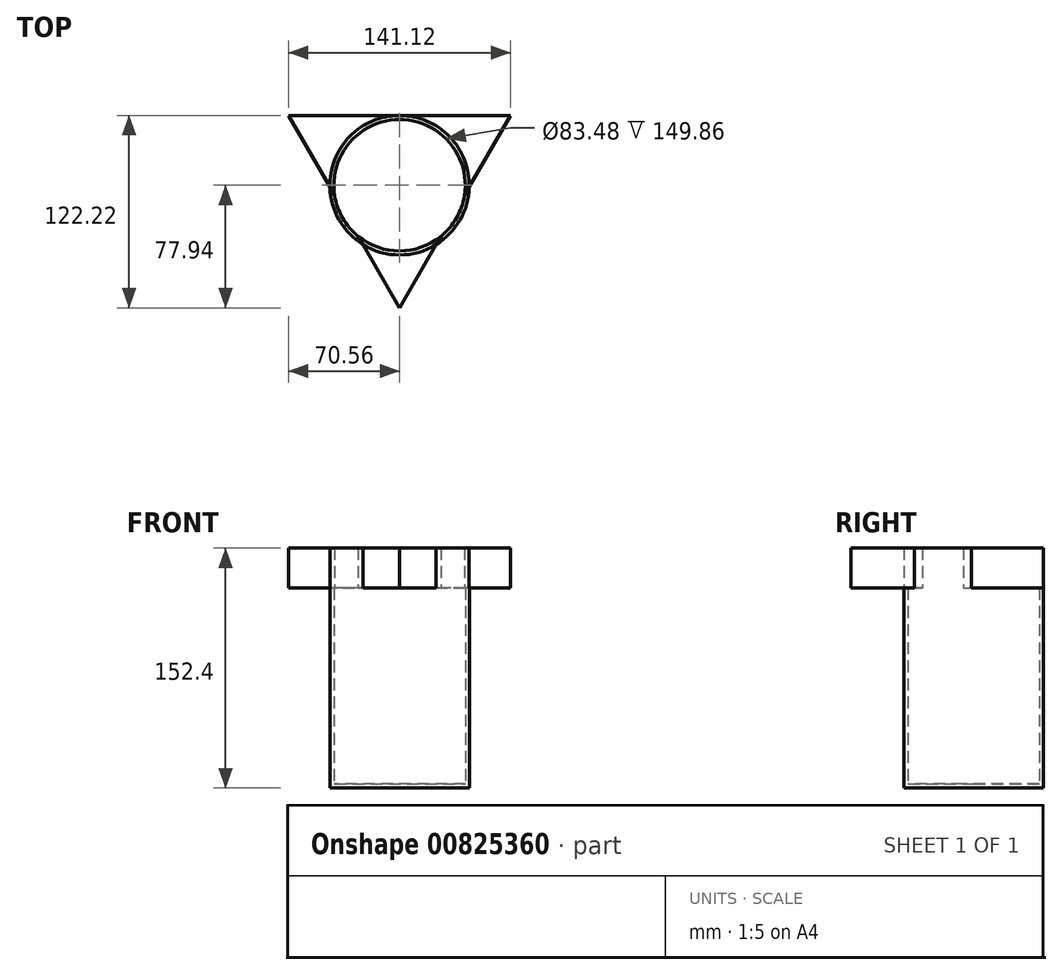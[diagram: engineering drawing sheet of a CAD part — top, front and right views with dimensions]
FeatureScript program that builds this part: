
annotation { "Feature Type Name" : "Feature", "Feature Type Description" : "" }
export const myFeature = defineFeature(function(context is Context, id is Id, definition is map)
    precondition{}
    {
        {
            var Q0;
            Q0=qCreatedBy(makeId("Top.planeOp"),FACE);
            var sketch = newSketch(context, id + "F0", { "sketchPlane" : qUnion([Q0])});
            skCircle(sketch, "E0", {"center": v(0, 0) * mm, "radius": 44.28 * mm});
            skSolve(sketch);
        }
        {
            var Q0;
            Q0 = qSketchRegion(id + "F0", true);
            extrude(context, id + "F1", {"entities" : qUnion([Q0]), "depth" : 127 * mm, "offsetDistance" : 25.4 * mm});
        }
        {
            var Q0;
            Q0=makeQuery(id+"F1.opExtrude","CAP_FACE",FACE,{"disambiguationData":[OSD([sQuery(id+"F0.wireOp",EDGE,"E0")])],"isStart":false});
            shell(context, id + "F2", {"entities" : qUnion([Q0]), "thickness" : 2.54 * mm});
        }
        {
            var Q0;
            Q0=makeQuery(id+"F1.opExtrude","CAP_FACE",FACE,{"disambiguationData":[OSD([sQuery(id+"F0.wireOp",EDGE,"E0")])],"isStart":false});
            var sketch = newSketch(context, id + "F3", { "sketchPlane" : qUnion([Q0])});
            skCircle(sketch, "E1.cCircle", {"center": v(0, 3.54) * mm, "radius": 40.74 * mm, "construction": true});
            skLineSegment(sketch, "E1.0", {"start": v(-70.56, 44.28) * mm, "end": v(70.56, 44.28) * mm});
            skLineSegment(sketch, "E1.1", {"start": v(70.56, 44.28) * mm, "end": v(0, -77.94) * mm});
            skLineSegment(sketch, "E1.2", {"start": v(0, -77.94) * mm, "end": v(-70.56, 44.28) * mm});
            skPoint(sketch, "E1.0.midPoint", {"position": v(0, 44.28) * mm});
            skSolve(sketch);
        }
        {
            var Q0;
            {var subQ0=sQuery(id+"F3.wireOp",EDGE,"E1.2");var subQ1=sQuery(id+"F3.wireOp",EDGE,"E1.1");var subQ2=makeQuery(id+"F3.imprint","INTERSECT",VERTEX,{"derivedFrom":[subQ1,subQ0]});Q0=makeQuery(id+"F3.imprint","IMPRINT",FACE,{"disambiguationData":[TD([[makeQuery(id+"F3.imprint","IMPRINT",EDGE,{"disambiguationData":[TD([[subQ2,1.0]])],"derivedFrom":subQ1}),-1.0]])]});}
            var Q1;
            {var subQ0=sQuery(id+"F3.wireOp",EDGE,"E1.2");var subQ1=sQuery(id+"F3.wireOp",EDGE,"E1.0");var subQ2=makeQuery(id+"F3.imprint","INTERSECT",VERTEX,{"derivedFrom":[subQ1,subQ0]});Q1=makeQuery(id+"F3.imprint","IMPRINT",FACE,{"disambiguationData":[TD([[makeQuery(id+"F3.imprint","IMPRINT",EDGE,{"disambiguationData":[TD([[subQ2,-1.0]])],"derivedFrom":subQ1}),-1.0]])]});}
            var Q2;
            {var subQ0=sQuery(id+"F3.wireOp",EDGE,"E1.1");var subQ1=sQuery(id+"F3.wireOp",EDGE,"E1.0");var subQ2=makeQuery(id+"F3.imprint","INTERSECT",VERTEX,{"derivedFrom":[subQ1,subQ0]});Q2=makeQuery(id+"F3.imprint","IMPRINT",FACE,{"disambiguationData":[TD([[makeQuery(id+"F3.imprint","IMPRINT",EDGE,{"disambiguationData":[TD([[subQ2,1.0]])],"derivedFrom":subQ1}),-1.0]])]});}
            var Q3;
            {var subQ0=sQuery(id+"F3.wireOp",EDGE,"E1.2");var subQ1=sQuery(id+"F0.wireOp",EDGE,"E0");var subQ2=makeQuery(id+"F1.opExtrude","CAP_EDGE",EDGE,{"disambiguationData":[OSD([subQ1])],"isStart":false});var subQ3=makeQuery(id+"F3.imprint","INTERSECT",VERTEX,{"disambiguationData":[OD(0.0)],"derivedFrom":[subQ2,subQ0]});Q3=makeQuery(id+"F3.imprint","IMPRINT",FACE,{"disambiguationData":[TD([[makeQuery(id+"F3.imprint","IMPRINT",EDGE,{"disambiguationData":[TD([[subQ3,1.0]])],"derivedFrom":subQ2}),1.0]])]});}
            var Q4;
            {var subQ0=sQuery(id+"F3.wireOp",EDGE,"E1.1");var subQ1=sQuery(id+"F0.wireOp",EDGE,"E0");var subQ2=makeQuery(id+"F1.opExtrude","CAP_EDGE",EDGE,{"disambiguationData":[OSD([subQ1])],"isStart":false});var subQ3=makeQuery(id+"F3.imprint","INTERSECT",VERTEX,{"disambiguationData":[OD(0.0)],"derivedFrom":[subQ2,subQ0]});Q4=makeQuery(id+"F3.imprint","IMPRINT",FACE,{"disambiguationData":[TD([[makeQuery(id+"F3.imprint","IMPRINT",EDGE,{"disambiguationData":[TD([[subQ3,1.0]])],"derivedFrom":subQ2}),1.0]])]});}
            extrude(context, id + "F4", {"entities" : qUnion([Q0, Q1, Q2, Q3, Q4]), "operationType" : NewBodyOperationType.ADD, "depth" : 25.4 * mm, "offsetDistance" : 25.4 * mm});
        }
        {
            var Q0;
            {var subQ0=sQuery(id+"F3.wireOp",EDGE,"E1.1");var subQ1=sQuery(id+"F3.wireOp",EDGE,"E1.0");var subQ2=makeQuery(id+"F3.imprint","INTERSECT",VERTEX,{"derivedFrom":[subQ1,subQ0]});Q0=makeQuery(id+"F3.imprint","IMPRINT",FACE,{"disambiguationData":[TD([[makeQuery(id+"F3.imprint","IMPRINT",EDGE,{"disambiguationData":[TD([[subQ2,1.0]])],"derivedFrom":subQ1}),-1.0]])]});}
            var Q1;
            {var subQ0=sQuery(id+"F3.wireOp",EDGE,"E1.2");var subQ1=sQuery(id+"F3.wireOp",EDGE,"E1.0");var subQ2=makeQuery(id+"F3.imprint","INTERSECT",VERTEX,{"derivedFrom":[subQ1,subQ0]});Q1=makeQuery(id+"F3.imprint","IMPRINT",FACE,{"disambiguationData":[TD([[makeQuery(id+"F3.imprint","IMPRINT",EDGE,{"disambiguationData":[TD([[subQ2,-1.0]])],"derivedFrom":subQ1}),-1.0]])]});}
            var Q2;
            {var subQ0=sQuery(id+"F3.wireOp",EDGE,"E1.2");var subQ1=sQuery(id+"F3.wireOp",EDGE,"E1.1");var subQ2=makeQuery(id+"F3.imprint","INTERSECT",VERTEX,{"derivedFrom":[subQ1,subQ0]});Q2=makeQuery(id+"F3.imprint","IMPRINT",FACE,{"disambiguationData":[TD([[makeQuery(id+"F3.imprint","IMPRINT",EDGE,{"disambiguationData":[TD([[subQ2,1.0]])],"derivedFrom":subQ1}),-1.0]])]});}
            extrude(context, id + "F5", {"entities" : qUnion([Q0, Q1, Q2]), "depth" : 25.4 * mm, "offsetDistance" : 25.4 * mm});
        }
    });
